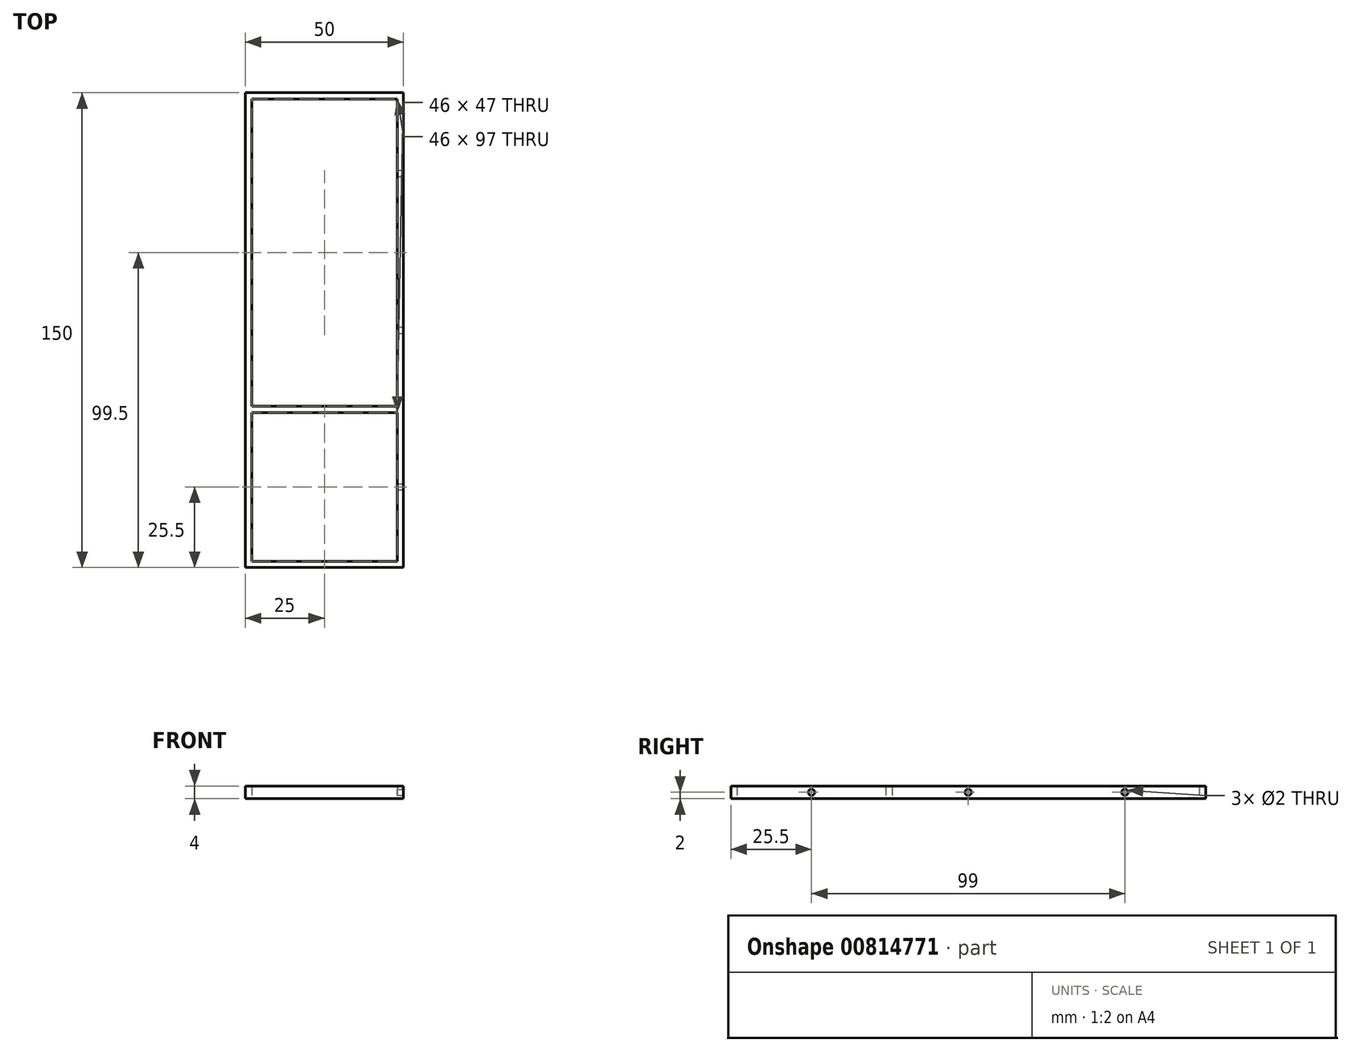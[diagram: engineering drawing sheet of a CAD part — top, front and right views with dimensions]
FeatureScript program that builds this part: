
annotation { "Feature Type Name" : "Feature", "Feature Type Description" : "" }
export const myFeature = defineFeature(function(context is Context, id is Id, definition is map)
    precondition{}
    {
        {
            var Q0;
            Q0=qCreatedBy(makeId("Top.planeOp"),FACE);
            var sketch = newSketch(context, id + "F0", { "sketchPlane" : qUnion([Q0])});
            skLineSegment(sketch, "E0.bottom", {"start": v(-25, 75) * mm, "end": v(25, 75) * mm});
            skLineSegment(sketch, "E0.top", {"start": v(-25, -75) * mm, "end": v(25, -75) * mm});
            skLineSegment(sketch, "E0.left", {"start": v(-25, 75) * mm, "end": v(-25, -75) * mm});
            skLineSegment(sketch, "E0.right", {"start": v(25, 75) * mm, "end": v(25, -75) * mm});
            skPoint(sketch, "E0.middle", {"position": v(0, 0) * mm});
            skLineSegment(sketch, "E1.bottom", {"start": v(-23, -73) * mm, "end": v(23, -73) * mm});
            skLineSegment(sketch, "E1.top", {"start": v(-23, -26) * mm, "end": v(23, -26) * mm});
            skLineSegment(sketch, "E1.left", {"start": v(-23, -73) * mm, "end": v(-23, -26) * mm});
            skLineSegment(sketch, "E1.right", {"start": v(23, -73) * mm, "end": v(23, -26) * mm});
            skPoint(sketch, "E1.middle", {"position": v(0, -49.5) * mm});
            skLineSegment(sketch, "E2.bottom", {"start": v(-23, 73) * mm, "end": v(23, 73) * mm});
            skLineSegment(sketch, "E2.top", {"start": v(-23, -24) * mm, "end": v(23, -24) * mm});
            skLineSegment(sketch, "E2.left", {"start": v(-23, 73) * mm, "end": v(-23, -24) * mm});
            skLineSegment(sketch, "E2.right", {"start": v(23, 73) * mm, "end": v(23, -24) * mm});
            skPoint(sketch, "E2.middle", {"position": v(0, 24.5) * mm});
            skSolve(sketch);
        }
        {
            var Q0;
            Q0=qSketchRegion(id+"F0",true);
            extrude(context, id + "F1", {"entities" : qUnion([Q0]), "depth" : 4 * mm, "offsetDistance" : 25 * mm});
        }
        {
            var Q0;
            Q0=makeQuery(id+"F1.opExtrude","SWEPT_FACE",FACE,{"disambiguationData":[OSD([sQuery(id+"F0.wireOp",EDGE,"E0.right")])]});
            var sketch = newSketch(context, id + "F2", { "sketchPlane" : qUnion([Q0])});
            skCircle(sketch, "E3", {"center": v(-49.5, 2) * mm, "radius": 1 * mm});
            skCircle(sketch, "E4", {"center": v(0, 2) * mm, "radius": 1 * mm});
            skCircle(sketch, "E5", {"center": v(49.5, 2) * mm, "radius": 1 * mm});
            skPoint(sketch, "E6", {"position": v(-24, 4) * mm});
            skLineSegment(sketch, "E7", {"start": v(-24, 4) * mm, "end": v(-24, 0) * mm});
            skSolve(sketch);
        }
        {
            var Q0;
            Q0=qSketchRegion(id+"F2",true);
            extrude(context, id + "F3", {"entities" : qUnion([Q0]), "operationType" : NewBodyOperationType.REMOVE, "oppositeDirection" : true, "depth" : 25 * mm, "offsetDistance" : 25 * mm});
        }
    });
